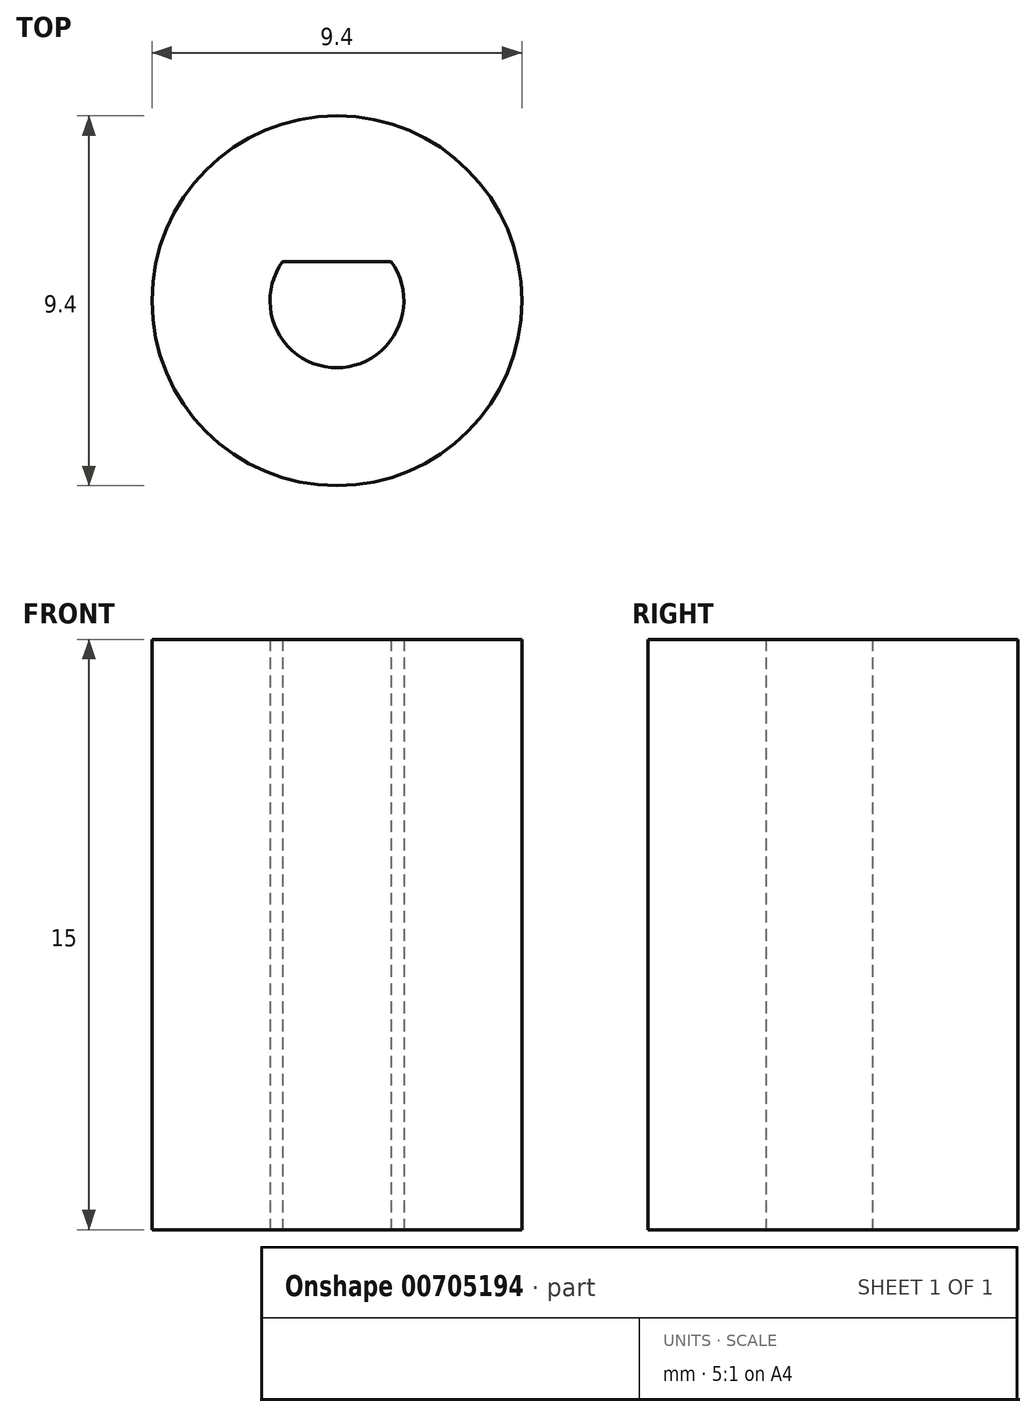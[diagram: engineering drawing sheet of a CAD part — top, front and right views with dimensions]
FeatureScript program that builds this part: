
annotation { "Feature Type Name" : "Feature", "Feature Type Description" : "" }
export const myFeature = defineFeature(function(context is Context, id is Id, definition is map)
    precondition{}
    {
        {
            var Q0;
            Q0=qCreatedBy(makeId("Top.planeOp"),FACE);
            var sketch = newSketch(context, id + "F0", { "sketchPlane" : qUnion([Q0])});
            skCircle(sketch, "E0", {"center": v(0, 0) * mm, "radius": 1.7 * mm});
            skCircle(sketch, "E1", {"center": v(0, 0) * mm, "radius": 4.7 * mm});
            skLineSegment(sketch, "E2", {"start": v(-1.37, 1) * mm, "end": v(1.37, 1) * mm});
            skSolve(sketch);
        }
        {
            var Q0;
            Q0=makeQuery(id+"F0.imprint","IMPRINT",FACE,{"disambiguationData":[TD([[makeQuery(id+"F0.imprint","IMPRINT",EDGE,{"derivedFrom":sQuery(id+"F0.wireOp",EDGE,"E1")}),1.0]])]});
            var Q1;
            {var subQ0=sQuery(id+"F0.wireOp",EDGE,"E2");Q1=makeQuery(id+"F0.imprint","IMPRINT",FACE,{"disambiguationData":[TD([[makeQuery(id+"F0.imprint","IMPRINT",EDGE,{"derivedFrom":subQ0}),1.0]])]});}
            extrude(context, id + "F1", {"entities" : qUnion([Q0, Q1]), "depth" : 15 * mm, "symmetric" : true});
        }
    });
